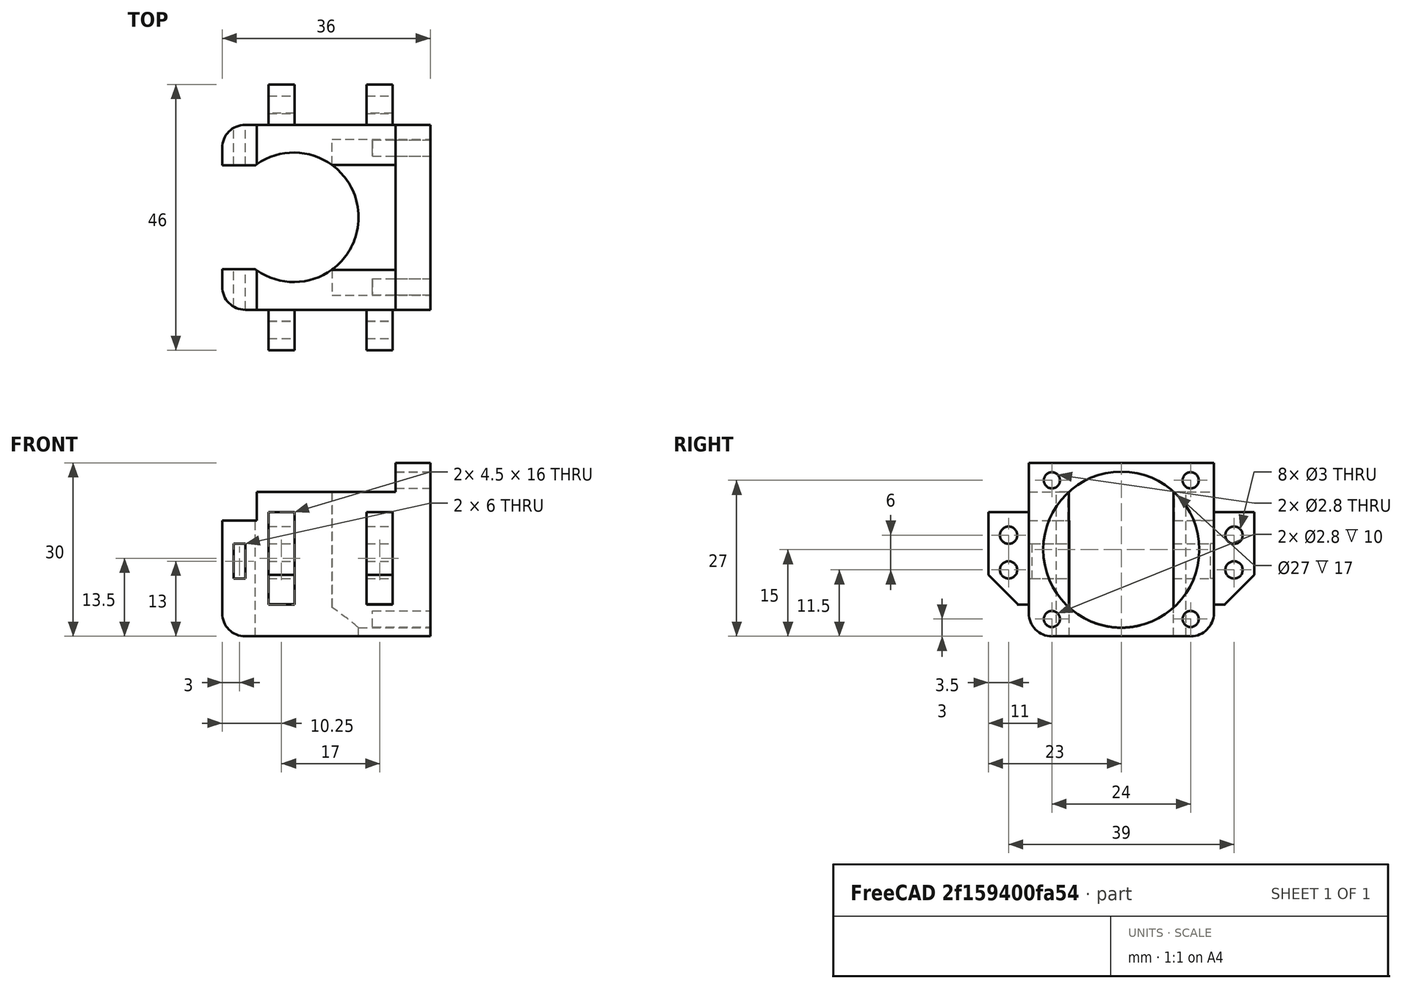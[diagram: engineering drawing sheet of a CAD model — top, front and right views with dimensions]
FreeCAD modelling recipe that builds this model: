
FCSTD DOCUMENT  (FreeCAD 0.15R4671 (Git))
Label: e3dv6
License: All rights reserved
LicenseURL: http://en.wikipedia.org/wiki/All_rights_reserved
objects: Part::Box×11, Part::Cylinder×10, Part::MultiFuse×6, Part::Fillet×4, Part::Cut×1
note: 32 computed .brp shape members not serialized (recipe doc carries the construction recipe); baked Part::Feature solids carry a one-line shape summary decoded from their .brp

FEATURE [Part::Box] Box  label="CubeMain"
  Height = 25
  Length = 24
  Width = 32
FEATURE [Part::Box] Box001  label="CubeFrontMask"
  Height = 30
  Length = 6
  Placement = pos=(24,0,0) rot=(0,0,1;0rad)
  Width = 32
FEATURE [Part::Cylinder] Cylinder  label="CylinderHeatSink"
  Angle = 360
  Height = 25
  Placement = pos=(6.4,16,0) rot=(0,0,1;0rad)
  Radius = 11.2
FEATURE [Part::Cylinder] Cylinder001  label="CylinderFan"
  Angle = 360
  Height = 18
  Placement = pos=(13,16,15) rot=(0,1,0;1.5708rad)
  Radius = 13.5
FEATURE [Part::Cylinder] Cylinder002  label="CylinderBL"
  Angle = 360
  Height = 20
  Placement = pos=(20,4,3) rot=(0,1,0;1.5708rad)
  Radius = 1.4
FEATURE [Part::Cylinder] Cylinder003  label="CylinderTL"
  Angle = 360
  Height = 20
  Placement = pos=(20,4,27) rot=(0,1,0;1.5708rad)
  Radius = 1.4
FEATURE [Part::Cylinder] Cylinder004  label="CylinderTB"
  Angle = 360
  Height = 20
  Placement = pos=(20,28,27) rot=(0,1,0;1.5708rad)
  Radius = 1.4
FEATURE [Part::Cylinder] Cylinder005  label="CylinderRB"
  Angle = 360
  Height = 20
  Placement = pos=(20,28,3) rot=(0,1,0;1.5708rad)
  Radius = 1.4
FEATURE [Part::MultiFuse] Fusion001  label="FusionFanScrews"
  Shapes = -> [Cylinder002,Cylinder003,Cylinder005,Cylinder004]
FEATURE [Part::Box] Box002  label="CubeZipTieL"
  Height = 20
  Length = 6
  Placement = pos=(-6,0,0) rot=(0,0,1;0rad)
  Width = 7
FEATURE [Part::Box] Box003  label="CubZipTieR"
  Height = 20
  Length = 6
  Placement = pos=(-6,25,0) rot=(0,0,1;0rad)
  Width = 7
FEATURE [Part::Box] Box004  label="CubeZipTieHor"
  Height = 6
  Length = 2
  Placement = pos=(-4,0,10) rot=(0,0,1;0rad)
  Width = 32
FEATURE [Part::Cylinder] Cylinder009
  Angle = 360
  Height = 40
  Placement = pos=(0,-3.5,12) rot=(0,1,0;1.5708rad)
  Radius = 1.5
FEATURE [Part::Cylinder] Cylinder010
  Angle = 360
  Height = 40
  Placement = pos=(0,-3.5,6) rot=(0,1,0;1.5708rad)
  Radius = 1.5
FEATURE [Part::Box] Box005  label="Cube005"
  Height = 16
  Length = 4.5
  Placement = pos=(2,-7,0) rot=(0,0,1;0rad)
  Width = 7
FEATURE [Part::Box] Box006  label="Cube006"
  Height = 16
  Length = 4.5
  Placement = pos=(19,-7,0) rot=(0,0,1;0rad)
  Width = 7
FEATURE [Part::Box] Box007  label="Cube007"
  Height = 16
  Length = 4.5
  Placement = pos=(2,32,0) rot=(0,0,1;0rad)
  Width = 7
FEATURE [Part::Box] Box008  label="Cube008"
  Height = 16
  Length = 4.5
  Placement = pos=(19,32,0) rot=(0,0,1;0rad)
  Width = 7
FEATURE [Part::Cylinder] Cylinder011
  Angle = 360
  Height = 40
  Placement = pos=(0,35.5,12) rot=(0,1,0;1.5708rad)
  Radius = 1.5
FEATURE [Part::Cylinder] Cylinder012
  Angle = 360
  Height = 40
  Placement = pos=(0,35.5,6) rot=(0,1,0;1.5708rad)
  Radius = 1.5
FEATURE [Part::MultiFuse] Fusion004  label="FusionWingScrews"
  Placement = pos=(0,0,5.5) rot=(0,0,1;0rad)
  Shapes = -> [Cylinder009,Cylinder010,Cylinder011,Cylinder012]
FEATURE [Part::Box] Box009  label="Cube009"
  Height = 10
  Length = 22
  Placement = pos=(2,-9,-7) rot=(1,0,0;0.785398rad)
  Width = 10
FEATURE [Part::Box] Box010  label="Cube010"
  Height = 10
  Length = 22
  Placement = pos=(2,41,-7) rot=(1,0,0;0.785398rad)
  Width = 10
FEATURE [Part::MultiFuse] Fusion006  label="FusionWings"
  Placement = pos=(0,0,5.5) rot=(0,0,1;0rad)
  Shapes = -> [Box005,Box006,Box007,Box008]
FEATURE [Part::MultiFuse] Fusion005  label="FusionWingCuts"
  Placement = pos=(0,0,5.5) rot=(0,0,1;0rad)
  Shapes = -> [Box009,Box010]
FEATURE [Part::MultiFuse] Fusion  label="FusionCUTS"
  Shapes = -> [Fusion001,Fusion005,Fusion004,Box004,Cylinder,Cylinder001]
FEATURE [Part::MultiFuse] Fusion007  label="FusionMain"
  Shapes = -> [Box,Box002,Fusion006,Box003,Box001]
FEATURE [Part::Fillet] Fillet
  Base = -> Fusion007
  Edges = 1 edges r=4: [Edge86]
FEATURE [Part::Fillet] Fillet001
  Base = -> Fillet
  Edges = 1 edges r=4: [Edge11]
FEATURE [Part::Fillet] Fillet002
  Base = -> Fillet001
  Edges = 1 edges r=4: [Edge66]
FEATURE [Part::Fillet] Fillet003
  Base = -> Fillet002
  Edges = 1 edges r=4: [Edge16]
FEATURE [Part::Cut] Cut  label="CutE3DV6"
  Base = -> Fillet003
  Tool = -> Fusion
